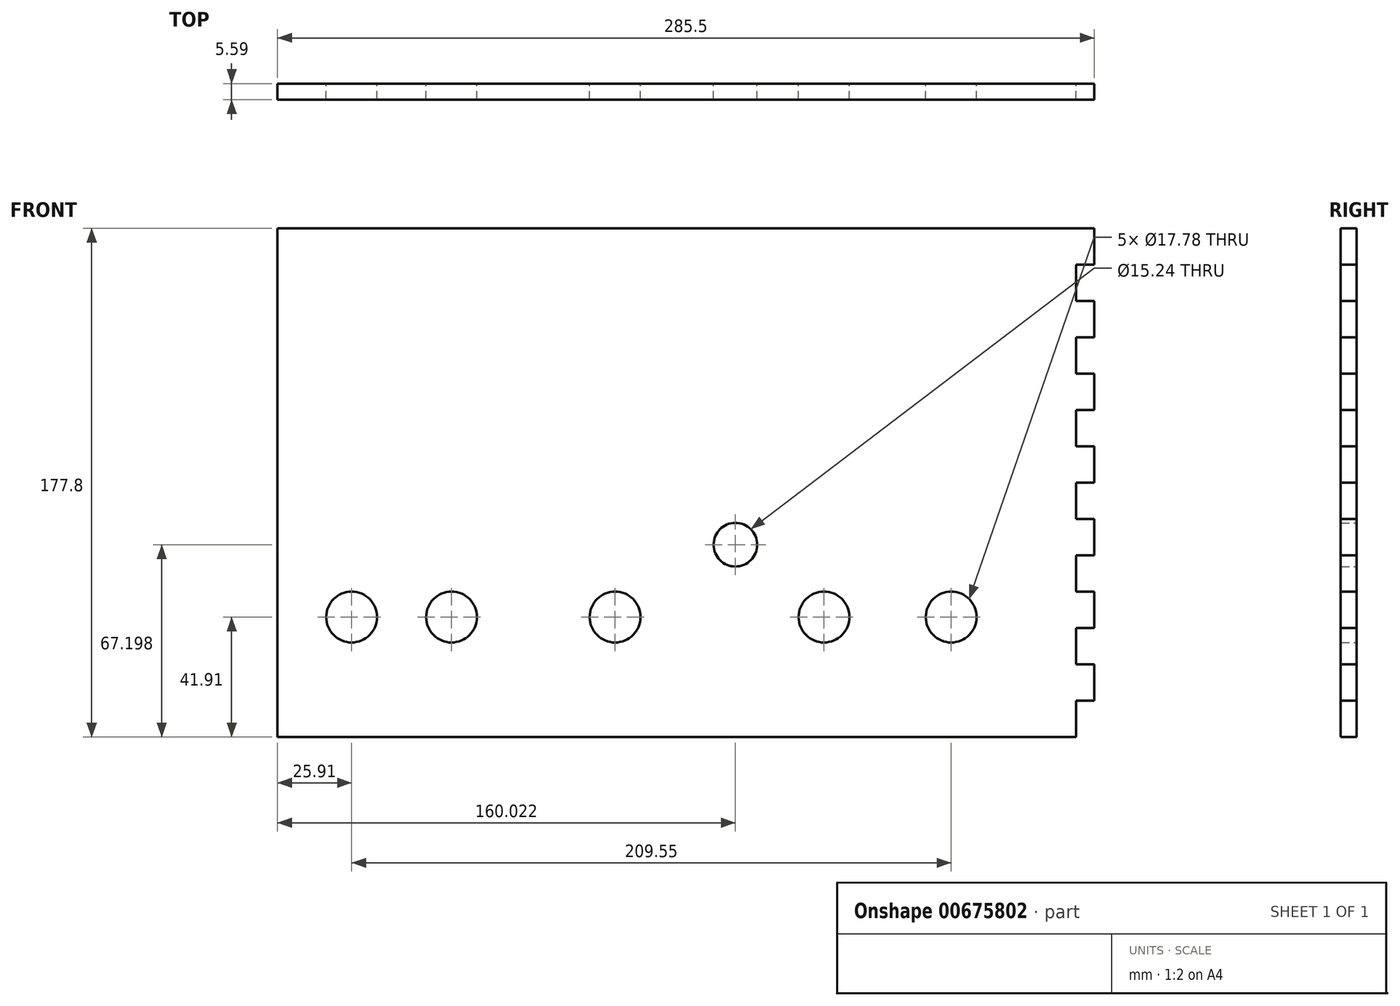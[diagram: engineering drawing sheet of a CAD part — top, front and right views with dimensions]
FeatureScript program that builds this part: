
annotation { "Feature Type Name" : "Feature", "Feature Type Description" : "" }
export const myFeature = defineFeature(function(context is Context, id is Id, definition is map)
    precondition{}
    {
        {
            var Q0;
            Q0=qCreatedBy(makeId("Front.planeOp"),FACE);
            var sketch = newSketch(context, id + "F0", { "sketchPlane" : qUnion([Q0])});
            skLineSegment(sketch, "E0.bottom", {"start": v(-142.75, 88.9) * mm, "end": v(142.75, 88.9) * mm});
            skLineSegment(sketch, "E0.top", {"start": v(-142.75, -88.9) * mm, "end": v(142.75, -88.9) * mm});
            skLineSegment(sketch, "E0.left", {"start": v(-142.75, 88.9) * mm, "end": v(-142.75, -88.9) * mm});
            skLineSegment(sketch, "E0.right", {"start": v(142.75, 88.9) * mm, "end": v(142.75, -88.9) * mm});
            skPoint(sketch, "E0.middle", {"position": v(0, 0) * mm});
            skSolve(sketch);
        }
        {
            var Q0;
            Q0 = qSketchRegion(id + "F0", true);
            extrude(context, id + "F1", {"entities" : qUnion([Q0]), "depth" : 5.6 * mm, "offsetDistance" : 25.4 * mm});
        }
        {
            var Q0;
            Q0=qCreatedBy(makeId("Front.planeOp"),FACE);
            var sketch = newSketch(context, id + "F2", { "sketchPlane" : qUnion([Q0])});
            skPoint(sketch, "E1", {"position": v(-116.84, -47) * mm});
            skPoint(sketch, "E2", {"position": v(-81.92, -47) * mm});
            skPoint(sketch, "E3", {"position": v(-24.77, -47) * mm});
            skPoint(sketch, "E4", {"position": v(48.26, -46.99) * mm});
            skPoint(sketch, "E5", {"position": v(92.7, -46.99) * mm});
            skSolve(sketch);
        }
        {
            var Q0;
            Q0=sQuery(id+"F2.wireOp",VERTEX,"E1");
            var Q1;
            Q1=sQuery(id+"F2.wireOp",VERTEX,"E2");
            var Q2;
            Q2=sQuery(id+"F2.wireOp",VERTEX,"E3");
            var Q3;
            Q3=sQuery(id+"F2.wireOp",VERTEX,"E4");
            var Q4;
            Q4=sQuery(id+"F2.wireOp",VERTEX,"E5");
            var Q5;
            Q5=makeQuery(id+"F1.opExtrude","SWEPT_BODY",BODY,{"disambiguationData":[OSD([sQuery(id+"F0.wireOp",EDGE,"E0.bottom"),sQuery(id+"F0.wireOp",EDGE,"E0.top"),sQuery(id+"F0.wireOp",EDGE,"E0.left"),sQuery(id+"F0.wireOp",EDGE,"E0.right")])]});
            hole(context, id + "F3", {"style" : HoleStyle.SIMPLE, "endStyle" : HoleEndStyle.THROUGH, "oppositeDirection" : true, "holeDiameter" : 17.78 * mm, "majorDiameter" : 6.35 * mm, "isTappedThrough" : true, "tappedDepth" : 12.7 * mm, "tapClearance" : 3, "locations" : qUnion([Q0, Q1, Q2, Q3, Q4]), "scope" : qUnion([Q5])});
        }
        {
            var Q0;
            Q0=qCreatedBy(makeId("Front.planeOp"),FACE);
            var sketch = newSketch(context, id + "F4", { "sketchPlane" : qUnion([Q0])});
            skLineSegment(sketch, "E6.bottom", {"start": v(142.75, 76.2) * mm, "end": v(136.4, 76.2) * mm});
            skLineSegment(sketch, "E6.top", {"start": v(142.75, 63.5) * mm, "end": v(136.4, 63.5) * mm});
            skLineSegment(sketch, "E6.left", {"start": v(142.75, 76.2) * mm, "end": v(142.75, 63.5) * mm});
            skLineSegment(sketch, "E6.right", {"start": v(136.4, 76.2) * mm, "end": v(136.4, 63.5) * mm});
            skLineSegment(sketch, "E7.bottom", {"start": v(142.75, 50.8) * mm, "end": v(136.4, 50.8) * mm});
            skLineSegment(sketch, "E7.top", {"start": v(142.75, 38.1) * mm, "end": v(136.4, 38.1) * mm});
            skLineSegment(sketch, "E7.left", {"start": v(142.75, 50.8) * mm, "end": v(142.75, 38.1) * mm});
            skLineSegment(sketch, "E7.right", {"start": v(136.4, 50.8) * mm, "end": v(136.4, 38.1) * mm});
            skLineSegment(sketch, "E8.bottom", {"start": v(142.75, 25.4) * mm, "end": v(136.4, 25.4) * mm});
            skLineSegment(sketch, "E8.top", {"start": v(142.75, 12.7) * mm, "end": v(136.4, 12.7) * mm});
            skLineSegment(sketch, "E8.left", {"start": v(142.75, 25.4) * mm, "end": v(142.75, 12.7) * mm});
            skLineSegment(sketch, "E8.right", {"start": v(136.4, 25.4) * mm, "end": v(136.4, 12.7) * mm});
            skLineSegment(sketch, "E9.bottom", {"start": v(142.75, 0) * mm, "end": v(136.4, 0) * mm});
            skLineSegment(sketch, "E9.top", {"start": v(142.75, -12.7) * mm, "end": v(136.4, -12.7) * mm});
            skLineSegment(sketch, "E9.left", {"start": v(142.75, 0) * mm, "end": v(142.75, -12.7) * mm});
            skLineSegment(sketch, "E9.right", {"start": v(136.4, 0) * mm, "end": v(136.4, -12.7) * mm});
            skLineSegment(sketch, "E10.bottom", {"start": v(142.75, -25.4) * mm, "end": v(136.4, -25.4) * mm});
            skLineSegment(sketch, "E10.top", {"start": v(142.75, -38.1) * mm, "end": v(136.4, -38.1) * mm});
            skLineSegment(sketch, "E10.left", {"start": v(142.75, -25.4) * mm, "end": v(142.75, -38.1) * mm});
            skLineSegment(sketch, "E10.right", {"start": v(136.4, -25.4) * mm, "end": v(136.4, -38.1) * mm});
            skLineSegment(sketch, "E11.bottom", {"start": v(142.75, -50.8) * mm, "end": v(136.4, -50.8) * mm});
            skLineSegment(sketch, "E11.top", {"start": v(142.75, -63.5) * mm, "end": v(136.4, -63.5) * mm});
            skLineSegment(sketch, "E11.left", {"start": v(142.75, -50.8) * mm, "end": v(142.75, -63.5) * mm});
            skLineSegment(sketch, "E11.right", {"start": v(136.4, -50.8) * mm, "end": v(136.4, -63.5) * mm});
            skLineSegment(sketch, "E12.bottom", {"start": v(142.75, -76.2) * mm, "end": v(136.4, -76.2) * mm});
            skLineSegment(sketch, "E12.top", {"start": v(142.75, -88.9) * mm, "end": v(136.4, -88.9) * mm});
            skLineSegment(sketch, "E12.left", {"start": v(142.75, -76.2) * mm, "end": v(142.75, -88.9) * mm});
            skLineSegment(sketch, "E12.right", {"start": v(136.4, -76.2) * mm, "end": v(136.4, -88.9) * mm});
            skSolve(sketch);
        }
        {
            var Q0;
            Q0 = qSketchRegion(id + "F4", true);
            extrude(context, id + "F5", {"entities" : qUnion([Q0]), "operationType" : NewBodyOperationType.REMOVE, "depth" : 25.4 * mm, "offsetDistance" : 25.4 * mm});
        }
        {
            var Q0;
            Q0=qCreatedBy(makeId("Front.planeOp"),FACE);
            var sketch = newSketch(context, id + "F6", { "sketchPlane" : qUnion([Q0])});
            skCircle(sketch, "E13", {"center": v(17.27, -21.7) * mm, "radius": 7.62 * mm});
            skSolve(sketch);
        }
        {
            var Q0;
            Q0 = qSketchRegion(id + "F6", true);
            extrude(context, id + "F7", {"entities" : qUnion([Q0]), "operationType" : NewBodyOperationType.REMOVE, "depth" : 25.4 * mm, "offsetDistance" : 25.4 * mm});
        }
    });
